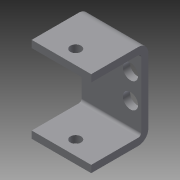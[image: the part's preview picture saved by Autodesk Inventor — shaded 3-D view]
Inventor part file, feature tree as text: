
AUTODESK INVENTOR PART (.ipt)
format: ipt  version: 2013 (Build 170138000, 138)  size: 128,512 bytes
history: native  units: in
note: dims shown in document units (in); Inventor stores cm internally (conversion verified against a paired STEP export)
features: sheet_metal_op x4, sketch x4, other x3, reference x2, extrude x1
ambient origin geometry x8: Origin, YZ Plane, XZ Plane, XY Plane, X Axis, Y Axis, Z Axis, Center Point
bodies: Solid1 (feature_tree)
feature tree (14):
  sheet_metal_op  "Face1"
  sheet_metal_op  "Flange1"
  extrude  "Extrusion1"  Depth=1.15in
  sketch  "Sketch1"  dims[d4=0.5788in d5=1.15in]
  other  "Plate1"
  sketch  "Sketch2"  dims[d6=0.125in]
  other  "Plate2"
  sheet_metal_op  "Bend1"
  sheet_metal_op  "Corner1"
  sketch  "Sketch3"  dims[d7=0.125in]
  sketch  "Sketch7"  dims[d8=0.0625in d9=0.25in d10=0.125in d11=1.0in d12=90.0deg d13=0.05in d14=0.5in d15=0.125in d16=0.125in d17=0.25in d18=0.1875in d19=2999.0in d20=0.0in d21=0.575in d26=0.125in d27=0.0in]
  reference  "Reference4"
  reference  "Reference5"
  other  "Cut3"
